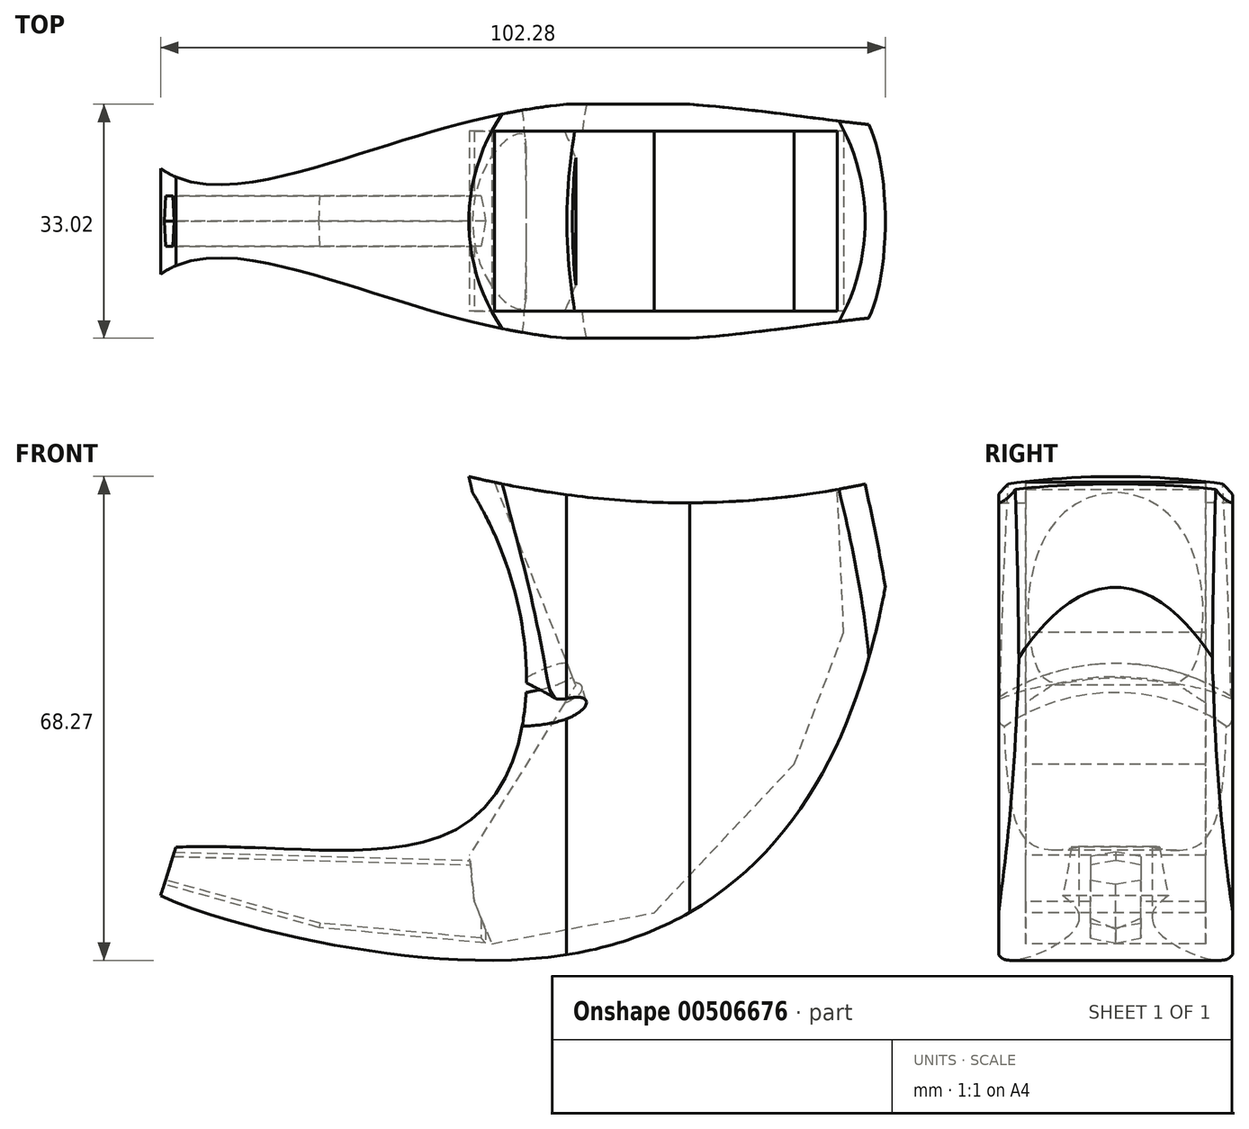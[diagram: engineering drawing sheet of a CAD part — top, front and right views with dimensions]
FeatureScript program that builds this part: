
annotation { "Feature Type Name" : "Feature", "Feature Type Description" : "" }
export const myFeature = defineFeature(function(context is Context, id is Id, definition is map)
    precondition{}
    {
        {
            var Q0;
            Q0=qCreatedBy(makeId("Front.planeOp"),FACE);
            var sketch = newSketch(context, id + "F0", { "sketchPlane" : qUnion([Q0])});
            skLineSegment(sketch, "E0", {"start": v(-28.97, 49.95) * mm, "end": v(32.98, 49.95) * mm});
            skFitSpline(sketch, "E1", {"points": [v(32.98, 49.95) * mm, v(-15.9, -18.2) * mm, v(-72.07, -8.94) * mm, v(-70.84, -2.84) * mm], "startDerivative": vector(-17.31, -261.1) * mm, "endDerivative": vector(-38.35, 134.12) * mm});
            skFitSpline(sketch, "E2", {"points": [v(-28.97, 49.95) * mm, v(-26.5, 1.86) * mm, v(-70.84, -2.84) * mm], "startDerivative": vector(70.07, -99.85) * mm, "endDerivative": vector(-101.5, -6.47) * mm});
            skFitSpline(sketch, "E3", {"points": [v(0, 49.95) * mm, v(0, 0) * mm, v(-70.47, -6.86) * mm], "startDerivative": vector(29.6, -131.51) * mm, "endDerivative": vector(-164.88, 13.68) * mm});
            skSolve(sketch);
        }
        {
            var Q0;
            Q0=qCreatedBy(makeId("Top.planeOp"),FACE);
            cPlane(context, id + "F1", {"entities" : qUnion([Q0]), "cplaneType" : CPlaneType.OFFSET, "offset" : 50.04 * mm, "width" : 152.4 * mm, "height" : 152.4 * mm});
        }
        {
            var Q0;
            Q0=qCreatedBy(makeId("Top.planeOp"),FACE);
            cPlane(context, id + "F2", {"entities" : qUnion([Q0]), "cplaneType" : CPlaneType.OFFSET, "offset" : 18.54 * mm, "oppositeDirection" : true, "width" : 152.4 * mm, "height" : 152.4 * mm});
        }
        {
            var Q0;
            Q0=qCreatedBy(id+"F1.planeOp",FACE);
            var sketch = newSketch(context, id + "F3", { "sketchPlane" : qUnion([Q0])});
            skCircle(sketch, "E4", {"center": v(0, 0) * mm, "radius": 27.85 * mm});
            skSolve(sketch);
        }
        {
            var Q0;
            Q0=makeQuery(id+"F3.imprint","IMPRINT",FACE,{"disambiguationData":[TD([[makeQuery(id+"F3.imprint","IMPRINT",EDGE,{"derivedFrom":sQuery(id+"F3.wireOp",EDGE,"Mz34haJp-2OX1-eP5z-FRbg-lCnBxig1CXiW")}),1.0]])]});
            var Q1;
            Q1=makeQuery(id+"F3.imprint","IMPRINT",FACE,{"disambiguationData":[TD([[makeQuery(id+"F3.imprint","IMPRINT",EDGE,{"derivedFrom":sQuery(id+"F3.wireOp",EDGE,"E4")}),1.0]])]});
            var Q2;
            Q2=sQuery(id+"F3.wireOp",EDGE,"E4");
            var Q3;
            Q3=sQuery(id+"F0.wireOp",EDGE,"E3");
            sweep(context, id + "F4", {"profiles" : qUnion([Q0, Q1]), "surfaceProfiles" : qUnion([Q2]), "path" : qUnion([Q3])});
        }
        {
            var Q0;
            Q0 = qSketchRegion(id + "F0", true);
            extrude(context, id + "F5", {"entities" : qUnion([Q0]), "operationType" : NewBodyOperationType.INTERSECT, "endBound" : BoundingType.SYMMETRIC, "oppositeDirection" : true, "depth" : 33.02 * mm});
        }
        {
            var Q0;
            Q0=qCreatedBy(id+"F1.planeOp",FACE);
            var sketch = newSketch(context, id + "F6", { "sketchPlane" : qUnion([Q0])});
            skFitSpline(sketch, "E5", {"points": [v(-71.31, -7.5) * mm, v(-16.01, -16.3) * mm, v(46.28, -14.3) * mm, v(54.46, -30.67) * mm, v(38.1, -61.01) * mm, v(-67.12, -55.22) * mm, v(-71.31, -7.5) * mm]});
            skFitSpline(sketch, "E6.MirrorC", {"points": [v(-71.31, 7.5) * mm, v(-16.01, 16.3) * mm, v(46.28, 14.3) * mm, v(54.46, 30.67) * mm, v(38.1, 61.01) * mm, v(-67.12, 55.22) * mm, v(-71.31, 7.5) * mm]});
            skSolve(sketch);
        }
        {
            var Q0;
            Q0=makeQuery(id+"F6.imprint","IMPRINT",FACE,{"disambiguationData":[TD([[makeQuery(id+"F6.imprint","IMPRINT",EDGE,{"derivedFrom":sQuery(id+"F6.wireOp",EDGE,"E6.MirrorC")}),1.0]])]});
            var Q1;
            Q1=makeQuery(id+"F6.imprint","IMPRINT",FACE,{"disambiguationData":[TD([[makeQuery(id+"F6.imprint","IMPRINT",EDGE,{"derivedFrom":sQuery(id+"F6.wireOp",EDGE,"E5")}),-1.0]])]});
            var Q2;
            Q2=sQuery(id+"F6.wireOp",EDGE,"E6.MirrorC");
            var Q3;
            Q3=sQuery(id+"F6.wireOp",EDGE,"E5");
            extrude(context, id + "F7", {"entities" : qUnion([Q0, Q1]), "operationType" : NewBodyOperationType.REMOVE, "surfaceEntities" : qUnion([Q2, Q3]), "oppositeDirection" : true, "depth" : 77.47 * mm, "offsetDistance" : 25.4 * mm});
        }
        {
            var Q0;
            Q0=qCreatedBy(makeId("Front.planeOp"),FACE);
            var sketch = newSketch(context, id + "F8", { "sketchPlane" : qUnion([Q0])});
            skLineSegment(sketch, "E7", {"start": v(24.16, 50.25) * mm, "end": v(-24.75, 50.25) * mm});
            skLineSegment(sketch, "E8", {"start": v(-24.75, 50.25) * mm, "end": v(-12.64, 20.1) * mm});
            skLineSegment(sketch, "E9", {"start": v(-12.64, 20.1) * mm, "end": v(-27.65, -3.9) * mm});
            skLineSegment(sketch, "E10", {"start": v(-26.95, -10.44) * mm, "end": v(-24.52, -16.4) * mm});
            skLineSegment(sketch, "E11", {"start": v(-24.52, -16.4) * mm, "end": v(-1.56, -12) * mm});
            skLineSegment(sketch, "E12", {"start": v(-1.56, -12) * mm, "end": v(18.2, 8.96) * mm});
            skLineSegment(sketch, "E13", {"start": v(18.2, 8.96) * mm, "end": v(25.19, 27.53) * mm});
            skLineSegment(sketch, "E14", {"start": v(25.19, 27.53) * mm, "end": v(24.16, 50.25) * mm});
            skLineSegment(sketch, "E15", {"start": v(-26.95, -10.44) * mm, "end": v(-27.65, -3.9) * mm});
            skSolve(sketch);
        }
        {
            var Q0;
            Q0 = qSketchRegion(id + "F8", true);
            extrude(context, id + "F9", {"entities" : qUnion([Q0]), "operationType" : NewBodyOperationType.REMOVE, "endBound" : BoundingType.SYMMETRIC, "oppositeDirection" : true, "depth" : 25.4 * mm, "offsetDistance" : 25.4 * mm});
        }
        {
            var Q0;
            Q0=qCreatedBy(makeId("Front.planeOp"),FACE);
            var sketch = newSketch(context, id + "F10", { "sketchPlane" : qUnion([Q0])});
            skLineSegment(sketch, "E16", {"start": v(-72.37, -3.35) * mm, "end": v(-25.36, -4.7) * mm});
            skLineSegment(sketch, "E17", {"start": v(-25.36, -4.7) * mm, "end": v(-25.36, -16.28) * mm});
            skLineSegment(sketch, "E18", {"start": v(-25.36, -16.28) * mm, "end": v(-48.87, -14.1) * mm});
            skLineSegment(sketch, "E19", {"start": v(-48.87, -14.1) * mm, "end": v(-72.87, -7.38) * mm});
            skLineSegment(sketch, "E20", {"start": v(-72.87, -7.38) * mm, "end": v(-72.37, -3.35) * mm});
            skSolve(sketch);
        }
        {
            var Q0;
            Q0 = qSketchRegion(id + "F10", true);
            extrude(context, id + "F11", {"entities" : qUnion([Q0]), "operationType" : NewBodyOperationType.REMOVE, "endBound" : BoundingType.SYMMETRIC, "depth" : 7.11 * mm, "hasDraft" : true, "draftAngle" : 10 * degree, "draftPullDirection" : true});
        }
        {
            var Q0;
            Q0=qCreatedBy(makeId("Front.planeOp"),FACE);
            var sketch = newSketch(context, id + "F12", { "sketchPlane" : qUnion([Q0])});
            skFitSpline(sketch, "E21", {"points": [v(49.26, 62.3) * mm, v(0, 45.87) * mm, v(-54.18, 65.98) * mm, v(49.26, 62.3) * mm]});
            skSolve(sketch);
        }
        {
            var Q0;
            Q0=makeQuery(id+"F12.imprint","IMPRINT",FACE,{"disambiguationData":[TD([[makeQuery(id+"F12.imprint","IMPRINT",EDGE,{"derivedFrom":sQuery(id+"F12.wireOp",EDGE,"E21")}),-1.0]])]});
            extrude(context, id + "F13", {"entities" : qUnion([Q0]), "operationType" : NewBodyOperationType.REMOVE, "endBound" : BoundingType.SYMMETRIC, "depth" : 55.37 * mm, "offsetDistance" : 25.4 * mm});
        }
    });
